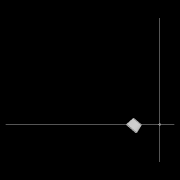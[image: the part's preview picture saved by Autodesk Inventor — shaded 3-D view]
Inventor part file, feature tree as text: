
AUTODESK INVENTOR PART (.ipt)
format: ipt  version: 2022.2 (Build 262287010, 287A)  size: 603,136 bytes
history: native  units: mm
features: extrude x19, sketch x18, pattern_circular x15, other x14, revolve x7, hole x7, move_body x4, fillet x2, draft x2
ambient origin geometry x8: Origin, YZ Plane, XZ Plane, XY Plane, X Axis, Y Axis, Z Axis, Center Point
bodies: Solid1 (feature_tree), Solid2 (feature_tree), Solid3 (feature_tree), Solid4 (feature_tree), Solid5 (feature_tree)
feature tree (88):
  sketch  "Sketch7"  dims[d21=0.5mm]
  other  "Roller1"
  other  "Roller2"
  sketch  "Sketch22"  dims[d39=0.05mm]
  sketch  "Sketch2"  dims[d17=0.05mm]
  sketch  "Sketch23"  dims[d41=0.05mm]
  other  "RevRoller1"
  fillet  "Fillet1"  Radius=0.05mm
  pattern_circular  "Circular Pattern13"  Count=6  [1 undecoded]
  move_body  "Move Body7"
  revolve  "Revolution13"  Angle=30.0deg
  fillet  "Fillet3"  [1 undecoded]
  pattern_circular  "Circular Pattern14"  [2 undecoded]
  move_body  "Move Body6"
  revolve  "Revolution14"  [1 undecoded]
  other  "OuterRim_Top2"
  other  "OuterRim_Bottom2"
  extrude  "Extrusion9"  TaperAngle=90.0deg  [1 undecoded]
  sketch  "Sketch24"  dims[d42=0.5mm]
  extrude  "Extrusion10"  Depth=0.5mm
  extrude  "Extrusion11"  Depth=0.5mm
  pattern_circular  "Circular Pattern15"  [2 undecoded]
  sketch  "Sketch25"  dims[d43=0.5mm]
  extrude  "Extrusion12"  Depth=0.5mm
  extrude  "Extrusion14"  Depth=0.5mm
  extrude  "Extrusion15"  Depth=0.5mm
  pattern_circular  "Circular Pattern16"  [2 undecoded]
  extrude  "Extrusion16"  Depth=0.5mm
  extrude  "Extrusion17"  Depth=0.5mm
  hole  "Hole9"  [1 undecoded]
  pattern_circular  "Circular Pattern17"  [2 undecoded]
  sketch  "Sketch27"  dims[d45=0.5mm]
  hole  "Hole10"  [1 undecoded]
  hole  "Hole11"  [1 undecoded]
  pattern_circular  "Circular Pattern18"  [2 undecoded]
  extrude  "Extrusion18"  Depth=0.5mm
  extrude  "Extrusion19"  Depth=0.5mm
  pattern_circular  "Circular Pattern19"  [2 undecoded]
  sketch  "Sketch28"  dims[d46=0.5mm d47=0.5mm d48=2.0mm d50=90.0deg d56=14.029612mm d57=4.025mm d90=16.473921mm d107=0.05mm d108=0.05mm d109=0.05mm d110=0.05mm d112=0.5mm d113=0.5mm d114=0.5mm d115=14.644822mm d116=14.607374mm d117=1.0mm d118=0.05mm d119=0.05mm d120=0.05mm d121=0.05mm d122=0.5mm d123=0.5mm d124=14.644822mm d125=14.607374mm d126=1.0mm d127=90.0deg d128=30.0deg d129=90.0deg d167=8.972256mm d173=10.814812mm d201=55.5mm d202=90.0deg d203=90.0deg d204=90.0deg d218=55.5mm d226=5.4mm d232=0.0mm d233=3600.0mm d234=10.502mm d235=0.0mm d243=1.902mm d244=0.0mm d246=2.75mm d247=5.251mm d248=0.0mm d249=3.0mm d250=0.0mm d251=90.0mm d252=360.0deg d254=2.75mm d255=3.0mm d256=5.251mm d257=0.0mm d258=3.0mm d259=0.0mm d260=90.0mm d261=360.0deg d277=76.5mm d281=73.5mm d282=24.65mm d283=6.0mm d284=4.0mm d285=2.0mm d286=90.0deg d287=5.251mm d288=0.0mm d289=60.0mm d290=360.0deg d292=0.436332mm d293=60.0mm d294=90.0mm d295=3.0mm d296=6.0mm d297=5.5mm d298=3.0mm d299=90.0deg d300=5.251mm d301=0.0mm d302=60.0mm d303=360.0deg d305=30.0deg d306=73.5mm d307=24.65mm d308=6.0mm d309=5.5mm d310=3.0mm d311=90.0deg d312=5.251mm d313=0.0mm d314=60.0mm d315=360.0deg d317=90.0mm d318=60.0mm d319=30.0deg d320=5.4mm d321=5.4mm d322=3.0mm d323=6.0mm d324=5.5mm d325=3.0mm d326=90.0deg d327=5.251mm d328=0.0mm d329=2.4mm d330=0.0mm d331=60.0mm d332=360.0deg d343=17.307186mm d344=17.309884mm d345=0.025mm d346=0.025mm d347=0.1mm d348=0.1mm d349=17.309884mm d350=17.307186mm d351=0.025mm d352=0.025mm d354=0.1mm d355=17.307186mm d356=17.309884mm d357=1.0mm d358=90.0deg d359=0.5mm d360=60.0mm d361=360.0deg d363=30.0deg d367=8.1mm d369=4.014775mm d370=0.1mm d371=1.0mm d372=30.0deg d373=90.0deg d374=0.5mm d375=60.0mm d376=360.0deg d378=90.0deg d379=0.1mm d380=0.1mm d381=0.1mm d382=0.1mm d383=0.1mm d384=10.502mm d385=0.0mm d386=0.0mm d391=1.0mm d392=55.5mm d393=1.5mm d394=1.5mm d395=1.5mm d396=1.5mm d397=90.0deg d398=90.0deg d399=90.0deg d400=55.5mm d401=10.502mm d402=0.0mm d403=2.75mm d404=1.5mm d405=10.502mm d406=0.0mm d407=3.0mm d408=0.0mm d409=90.0mm d410=360.0deg d412=5.4mm d413=5.251mm d414=0.0mm d417=5.4mm d418=2.4mm d419=0.0mm d420=2.4mm d421=0.0mm d422=90.0mm d423=360.0deg d425=60.0mm d426=90.0mm d427=1.5mm d428=1.5mm d429=5.4mm d430=5.4mm d431=5.251mm d432=0.0mm d433=2.4mm d434=0.0mm d435=30.0deg d436=73.5mm d437=24.65mm d438=6.0mm d439=4.0mm d440=2.0mm d441=90.0deg d442=5.251mm d443=0.0mm d444=60.0mm d445=360.0deg d447=3.0mm d448=6.0mm d449=5.5mm d450=3.0mm d451=90.0deg d452=5.251mm d453=0.0mm d454=24.65mm d455=6.0mm d456=5.5mm d457=3.0mm d458=90.0deg d459=5.251mm d460=0.0mm d461=60.0mm d462=360.0deg d464=5.251mm d465=0.0mm d466=3.0mm d467=0.0mm d468=90.0mm d469=360.0deg d472=1.5mm d474=5.251mm d475=0.0mm d481=3.0mm d482=0.0mm d483=90.0mm d484=360.0deg d486=0.436332mm d49=0.872665mm d51=0.872665mm d52=0.872665mm d236=0.5mm d237=0.872665mm d238=0.5mm d239=0.872665mm d291=0.0625mm d415=0.5mm d416=0.872665mm d471=0.5mm d473=0.5mm]
  extrude  "Extrusion20"  Depth=0.5mm
  extrude  "Extrusion22"  Depth=0.5mm
  pattern_circular  "Circular Pattern21"  [2 undecoded]
  draft  "FaceDraft2"
  other  "InnerRim"
  other  "OuterRim_Top"
  other  "OuterRim_Bottom"
  extrude  "Extrusion2"  Depth=0.5mm
  sketch  "Sketch13"  dims[d24=0.5mm]
  extrude  "Extrusion3"  Depth=1.0mm
  sketch  "Sketch15"  dims[d29=360.0deg d30=60.0mm]
  extrude  "Extrusion4"  TaperAngle=90.0deg  [1 undecoded]
  extrude  "Extrusion5"  TaperAngle=30.0deg  [1 undecoded]
  pattern_circular  "Circular Pattern6"  Angle=90.0deg  [1 undecoded]
  sketch  "Sketch16"  dims[d31=360.0deg d35=30.0deg d36=90.0deg]
  extrude  "Extrusion6"  Depth=0.5mm
  extrude  "Extrusion7"  Depth=0.5mm
  pattern_circular  "Circular Pattern7"  [2 undecoded]
  hole  "Hole5"  [1 undecoded]
  pattern_circular  "Circular Pattern9"  Angle=90.0deg  [1 undecoded]
  draft  "FaceDraft1"
  hole  "Hole6"  [1 undecoded]
  pattern_circular  "Circular Pattern10"  [2 undecoded]
  hole  "Hole7"  [1 undecoded]
  pattern_circular  "Circular Pattern11"  Count=360  [1 undecoded]
  hole  "Hole8"  [1 undecoded]
  extrude  "Extrusion8"  TaperAngle=0.0deg  [1 undecoded]
  pattern_circular  "Circular Pattern12"  [2 undecoded]
  sketch  "Sketch8"  dims[d22=0.5mm]
  sketch  "Sketch9"  dims[d23=0.5mm]
  revolve  "Revolution4"  [1 undecoded]
  move_body  "Move Body4"
  revolve  "Revolution5"  [1 undecoded]
  sketch  "Sketch5"  dims[d19=0.5mm]
  sketch  "Sketch6"  dims[d20=0.5mm]
  revolve  "Revolution3"  [1 undecoded]
  sketch  "Sketch4"  dims[d18=0.05mm]
  revolve  "Revolution1"  [1 undecoded]
  pattern_circular  "Circular Pattern1"  [2 undecoded]
  move_body  "Move Body3"
  revolve  "Revolution2"  [1 undecoded]
  other  "2D Equation Curve1"
  sketch  "Sketch14"  dims[d28=2.0mm]
  other  "Work Axis1"
  other  "Work Axis2"
  other  "Work Axis3"
  other  "Work Axis4"
  other  "Work Axis5"
  sketch  "Sketch26"  dims[d44=0.5mm]
note: 44 required parameter values undecoded (feature->parameter linkage not recoverable at this tier; creation-order binding heuristic only, values carry confidence <= 0.55)